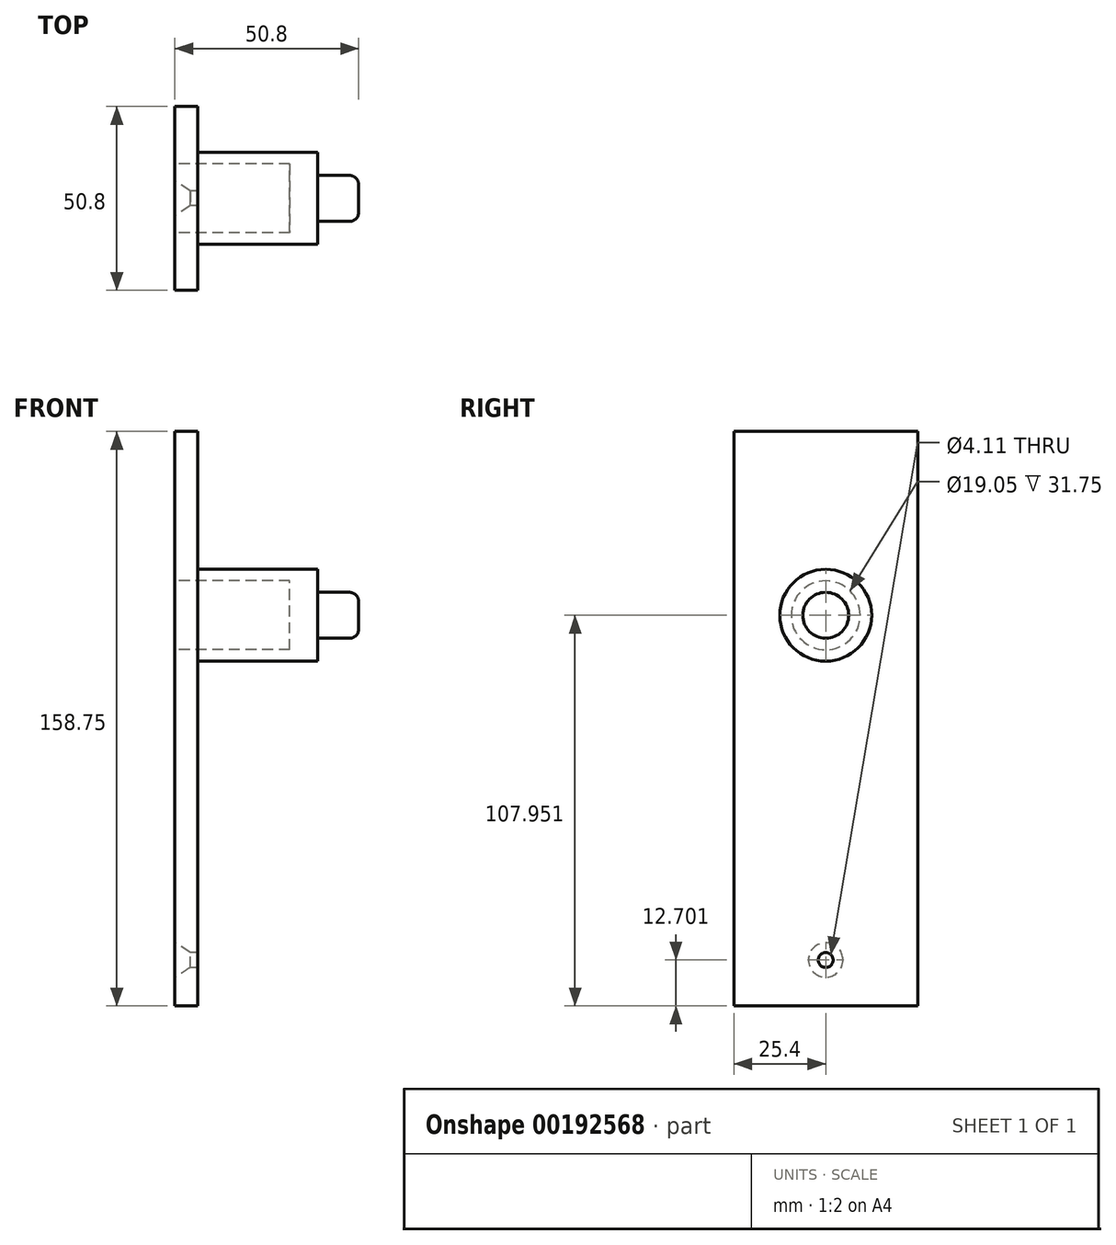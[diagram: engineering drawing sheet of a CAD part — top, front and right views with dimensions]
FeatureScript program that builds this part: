
annotation { "Feature Type Name" : "Feature", "Feature Type Description" : "" }
export const myFeature = defineFeature(function(context is Context, id is Id, definition is map)
    precondition{}
    {
        {
            var Q0;
            Q0=qCreatedBy(makeId("Right.planeOp"),FACE);
            var sketch = newSketch(context, id + "F0", { "sketchPlane" : qUnion([Q0])});
            skLineSegment(sketch, "E0.bottom", {"start": v(-25.4, 79.13) * mm, "end": v(25.4, 79.13) * mm});
            skLineSegment(sketch, "E0.top", {"start": v(-25.4, -79.62) * mm, "end": v(25.4, -79.62) * mm});
            skLineSegment(sketch, "E0.left", {"start": v(-25.4, 79.13) * mm, "end": v(-25.4, -79.62) * mm});
            skLineSegment(sketch, "E0.right", {"start": v(25.4, 79.13) * mm, "end": v(25.4, -79.62) * mm});
            skPoint(sketch, "E0.middle", {"position": v(0, -0.24) * mm});
            skLineSegment(sketch, "E1", {"start": v(0, 79.13) * mm, "end": v(0, 28.33) * mm});
            skPoint(sketch, "E1.endSnap0", {"position": v(0, 79.13) * mm});
            skLineSegment(sketch, "E2", {"start": v(0, 28.33) * mm, "end": v(0, -41.52) * mm});
            skLineSegment(sketch, "E3", {"start": v(0, -41.52) * mm, "end": v(0, -54.22) * mm});
            skLineSegment(sketch, "E4", {"start": v(0, -54.22) * mm, "end": v(0, -79.62) * mm});
            skCircle(sketch, "E5", {"center": v(0, 28.33) * mm, "radius": 12.7 * mm});
            skCircle(sketch, "E6", {"center": v(0, 28.33) * mm, "radius": 6.35 * mm});
            skCircle(sketch, "E7", {"center": v(0, -66.92) * mm, "radius": 2.06 * mm});
            skCircle(sketch, "E8", {"center": v(0, 28.33) * mm, "radius": 9.53 * mm});
            skSolve(sketch);
        }
        {
            var Q0;
            Q0 = qSketchRegion(id + "F0", true);
            extrude(context, id + "F1", {"entities" : qUnion([Q0]), "depth" : 6.35 * mm});
        }
        {
            var Q0;
            {var subQ0=sQuery(id+"F0.wireOp",EDGE,"E5");var subQ1=sQuery(id+"F0.wireOp",EDGE,"E1");var subQ2=makeQuery(id+"F0.imprint","INTERSECT",VERTEX,{"derivedFrom":[subQ1,subQ0]});Q0=makeQuery(id+"F0.imprint","IMPRINT",FACE,{"disambiguationData":[TD([[makeQuery(id+"F0.imprint","IMPRINT",EDGE,{"disambiguationData":[TD([[subQ2,-1.0]])],"derivedFrom":subQ1}),-1.0]])]});}
            var Q1;
            {var subQ0=sQuery(id+"F0.wireOp",EDGE,"E5");var subQ1=sQuery(id+"F0.wireOp",EDGE,"E1");var subQ2=makeQuery(id+"F0.imprint","INTERSECT",VERTEX,{"derivedFrom":[subQ1,subQ0]});Q1=makeQuery(id+"F0.imprint","IMPRINT",FACE,{"disambiguationData":[TD([[makeQuery(id+"F0.imprint","IMPRINT",EDGE,{"disambiguationData":[TD([[subQ2,-1.0]])],"derivedFrom":subQ1}),1.0]])]});}
            var Q2;
            {var subQ0=sQuery(id+"F0.wireOp",EDGE,"E8");var subQ1=sQuery(id+"F0.wireOp",EDGE,"E1");var subQ2=makeQuery(id+"F0.imprint","INTERSECT",VERTEX,{"derivedFrom":[subQ1,subQ0]});Q2=makeQuery(id+"F0.imprint","IMPRINT",FACE,{"disambiguationData":[TD([[makeQuery(id+"F0.imprint","IMPRINT",EDGE,{"disambiguationData":[TD([[subQ2,-1.0]])],"derivedFrom":subQ1}),-1.0]])]});}
            var Q3;
            {var subQ0=sQuery(id+"F0.wireOp",EDGE,"E8");var subQ1=sQuery(id+"F0.wireOp",EDGE,"E1");var subQ2=makeQuery(id+"F0.imprint","INTERSECT",VERTEX,{"derivedFrom":[subQ1,subQ0]});Q3=makeQuery(id+"F0.imprint","IMPRINT",FACE,{"disambiguationData":[TD([[makeQuery(id+"F0.imprint","IMPRINT",EDGE,{"disambiguationData":[TD([[subQ2,-1.0]])],"derivedFrom":subQ1}),1.0]])]});}
            extrude(context, id + "F2", {"entities" : qUnion([Q0, Q1, Q2, Q3]), "operationType" : NewBodyOperationType.ADD, "depth" : 39.5 * mm});
        }
        {
            var Q0;
            {var subQ0=sQuery(id+"F0.wireOp",EDGE,"E2");var subQ1=sQuery(id+"F0.wireOp",EDGE,"E1");var subQ2=makeQuery(id+"F0.imprint","INTERSECT",VERTEX,{"derivedFrom":[subQ1,subQ0]});Q0=makeQuery(id+"F0.imprint","IMPRINT",FACE,{"disambiguationData":[TD([[makeQuery(id+"F0.imprint","IMPRINT",EDGE,{"disambiguationData":[TD([[subQ2,1.0]])],"derivedFrom":subQ1}),-1.0]])]});}
            var Q1;
            {var subQ0=sQuery(id+"F0.wireOp",EDGE,"E2");var subQ1=sQuery(id+"F0.wireOp",EDGE,"E1");var subQ2=makeQuery(id+"F0.imprint","INTERSECT",VERTEX,{"derivedFrom":[subQ1,subQ0]});Q1=makeQuery(id+"F0.imprint","IMPRINT",FACE,{"disambiguationData":[TD([[makeQuery(id+"F0.imprint","IMPRINT",EDGE,{"disambiguationData":[TD([[subQ2,1.0]])],"derivedFrom":subQ1}),1.0]])]});}
            extrude(context, id + "F3", {"entities" : qUnion([Q0, Q1]), "operationType" : NewBodyOperationType.ADD, "depth" : 50.8 * mm});
        }
        {
            var Q0;
            Q0=makeQuery(id+"F3.opExtrude","CAP_EDGE",EDGE,{"disambiguationData":[OSD([sQuery(id+"F0.wireOp",EDGE,"E6")])],"isStart":false});
            fillet(context, id + "F4", {"entities" : qUnion([Q0]), "radius" : 2.54 * mm, "tangentPropagation" : true, "allowEdgeOverflow" : false});
        }
        {
            var Q0;
            Q0=makeQuery(id+"F1.opExtrude","CAP_EDGE",EDGE,{"disambiguationData":[OSD([sQuery(id+"F0.wireOp",EDGE,"E7")])],"isStart":true});
            chamfer(context, id + "F5", {"entities" : qUnion([Q0]), "chamferType" : ChamferType.TWO_OFFSETS, "width1" : 2.72 * mm, "oppositeDirection" : false, "width2" : 4.27 * mm, "tangentPropagation" : true});
        }
        {
            var Q0;
            {var subQ0=sQuery(id+"F0.wireOp",EDGE,"E8");var subQ1=sQuery(id+"F0.wireOp",EDGE,"E1");var subQ2=makeQuery(id+"F0.imprint","INTERSECT",VERTEX,{"derivedFrom":[subQ1,subQ0]});Q0=makeQuery(id+"F0.imprint","IMPRINT",FACE,{"disambiguationData":[TD([[makeQuery(id+"F0.imprint","IMPRINT",EDGE,{"disambiguationData":[TD([[subQ2,-1.0]])],"derivedFrom":subQ1}),-1.0]])]});}
            var Q1;
            {var subQ0=sQuery(id+"F0.wireOp",EDGE,"E2");var subQ1=sQuery(id+"F0.wireOp",EDGE,"E1");var subQ2=makeQuery(id+"F0.imprint","INTERSECT",VERTEX,{"derivedFrom":[subQ1,subQ0]});Q1=makeQuery(id+"F0.imprint","IMPRINT",FACE,{"disambiguationData":[TD([[makeQuery(id+"F0.imprint","IMPRINT",EDGE,{"disambiguationData":[TD([[subQ2,1.0]])],"derivedFrom":subQ1}),-1.0]])]});}
            var Q2;
            {var subQ0=sQuery(id+"F0.wireOp",EDGE,"E2");var subQ1=sQuery(id+"F0.wireOp",EDGE,"E1");var subQ2=makeQuery(id+"F0.imprint","INTERSECT",VERTEX,{"derivedFrom":[subQ1,subQ0]});Q2=makeQuery(id+"F0.imprint","IMPRINT",FACE,{"disambiguationData":[TD([[makeQuery(id+"F0.imprint","IMPRINT",EDGE,{"disambiguationData":[TD([[subQ2,1.0]])],"derivedFrom":subQ1}),1.0]])]});}
            var Q3;
            {var subQ0=sQuery(id+"F0.wireOp",EDGE,"E8");var subQ1=sQuery(id+"F0.wireOp",EDGE,"E1");var subQ2=makeQuery(id+"F0.imprint","INTERSECT",VERTEX,{"derivedFrom":[subQ1,subQ0]});Q3=makeQuery(id+"F0.imprint","IMPRINT",FACE,{"disambiguationData":[TD([[makeQuery(id+"F0.imprint","IMPRINT",EDGE,{"disambiguationData":[TD([[subQ2,-1.0]])],"derivedFrom":subQ1}),1.0]])]});}
            extrude(context, id + "F6", {"entities" : qUnion([Q0, Q1, Q2, Q3]), "operationType" : NewBodyOperationType.REMOVE, "depth" : 31.75 * mm});
        }
    });
